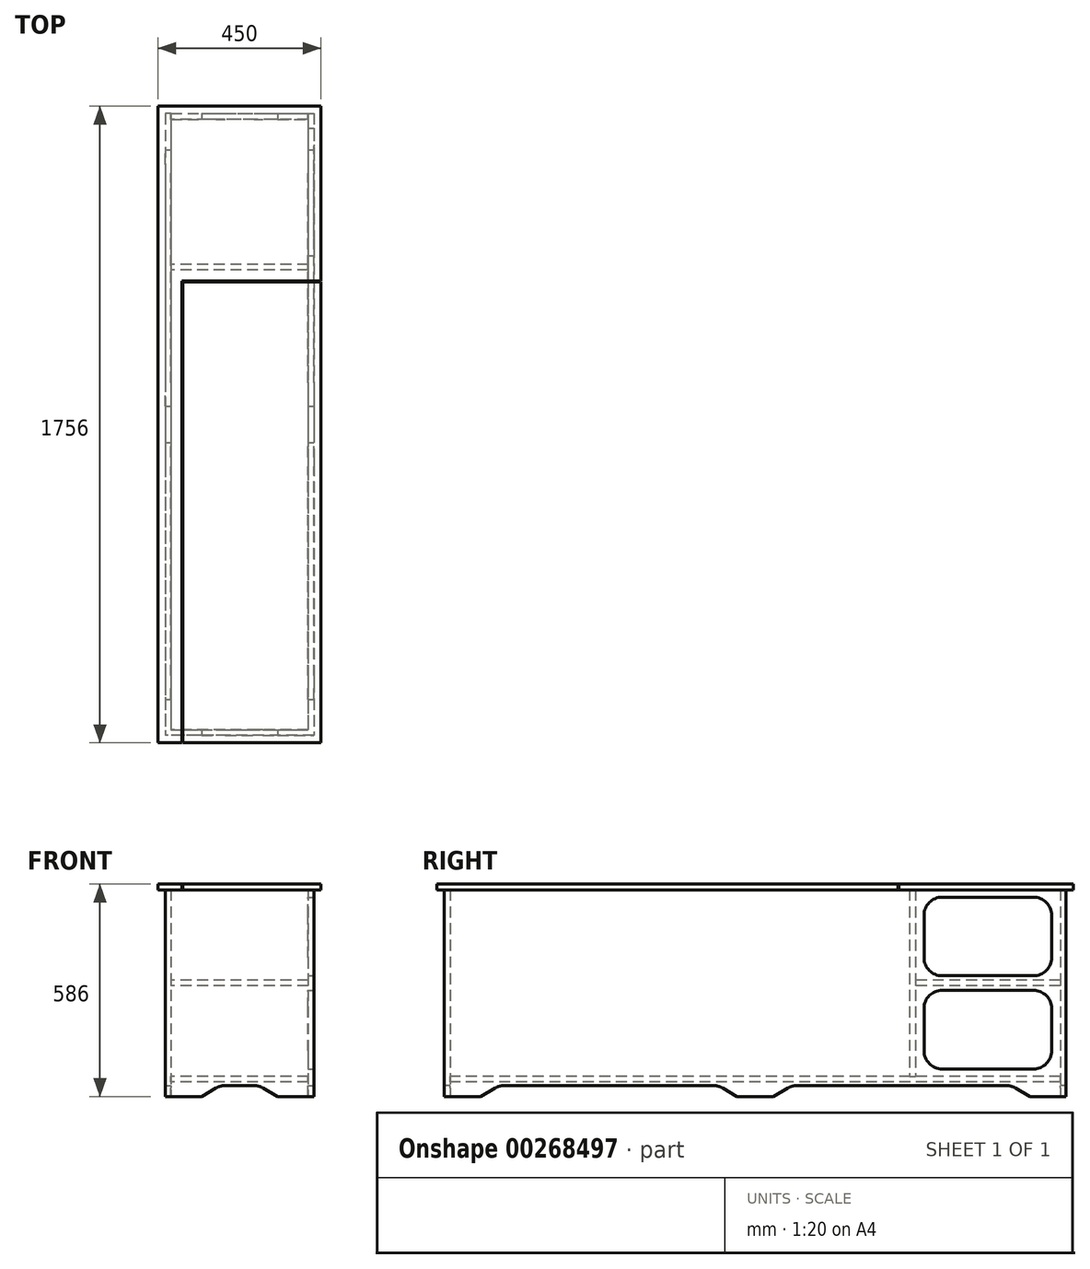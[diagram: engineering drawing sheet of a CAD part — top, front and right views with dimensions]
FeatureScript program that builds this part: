
annotation { "Feature Type Name" : "Feature", "Feature Type Description" : "" }
export const myFeature = defineFeature(function(context is Context, id is Id, definition is map)
    precondition{}
    {
        {
            var Q0;
            Q0=qCreatedBy(makeId("Right.planeOp"),FACE);
            var sketch = newSketch(context, id + "F0", { "sketchPlane" : qUnion([Q0])});
            skLineSegment(sketch, "E0.bottom", {"start": v(1716, 570) * mm, "end": v(0, 570) * mm});
            skLineSegment(sketch, "E0.top", {"start": v(1716, 0) * mm, "end": v(0, 0) * mm});
            skLineSegment(sketch, "E0.left", {"start": v(1716, 570) * mm, "end": v(1716, 0) * mm});
            skLineSegment(sketch, "E0.right", {"start": v(0, 570) * mm, "end": v(0, 0) * mm});
            skSolve(sketch);
        }
        {
            var Q0;
            Q0=makeQuery(id+"F0.imprint","IMPRINT",FACE,{"disambiguationData":[TD([[makeQuery(id+"F0.imprint","IMPRINT",EDGE,{"derivedFrom":sQuery(id+"F0.wireOp",EDGE,"E0.bottom")}),1.0]])]});
            extrude(context, id + "F1", {"entities" : qUnion([Q0]), "depth" : 16 * mm});
        }
        {
            var Q0;
            Q0=qCreatedBy(makeId("Right.planeOp"),FACE);
            cPlane(context, id + "F2", {"entities" : qUnion([Q0]), "cplaneType" : CPlaneType.OFFSET, "offset" : 410 * mm, "width" : 150 * mm, "height" : 150 * mm});
        }
        {
            var Q0;
            Q0=qCreatedBy(id+"F2.planeOp",FACE);
            var sketch = newSketch(context, id + "F3", { "sketchPlane" : qUnion([Q0])});
            skLineSegment(sketch, "E1.0", {"start": v(1716, 570) * mm, "end": v(0, 570) * mm});
            skLineSegment(sketch, "E2.0", {"start": v(0, 570) * mm, "end": v(0, 0) * mm});
            skLineSegment(sketch, "E3.0", {"start": v(1716, 0) * mm, "end": v(0, 0) * mm});
            skLineSegment(sketch, "E4.0", {"start": v(1716, 570) * mm, "end": v(1716, 0) * mm});
            skSolve(sketch);
        }
        {
            var Q0;
            Q0=makeQuery(id+"F3.imprint","IMPRINT",FACE,{"disambiguationData":[TD([[makeQuery(id+"F3.imprint","IMPRINT",EDGE,{"derivedFrom":sQuery(id+"F3.wireOp",EDGE,"E1.0")}),1.0]])]});
            extrude(context, id + "F4", {"entities" : qUnion([Q0]), "oppositeDirection" : true, "depth" : 16 * mm});
        }
        {
            var Q0;
            Q0=qCreatedBy(makeId("Front.planeOp"),FACE);
            var sketch = newSketch(context, id + "F5", { "sketchPlane" : qUnion([Q0])});
            skLineSegment(sketch, "E5.0", {"start": v(16, 570) * mm, "end": v(16, 0) * mm});
            skLineSegment(sketch, "E6.0", {"start": v(394, 570) * mm, "end": v(394, 0) * mm});
            skLineSegment(sketch, "E7", {"start": v(16, 570) * mm, "end": v(394, 570) * mm});
            skLineSegment(sketch, "E8", {"start": v(16, 0) * mm, "end": v(394, 0) * mm});
            skSolve(sketch);
        }
        {
            var Q0;
            Q0=makeQuery(id+"F5.imprint","IMPRINT",FACE,{"disambiguationData":[TD([[makeQuery(id+"F5.imprint","IMPRINT",EDGE,{"derivedFrom":sQuery(id+"F5.wireOp",EDGE,"E5.0")}),1.0]])]});
            extrude(context, id + "F6", {"entities" : qUnion([Q0]), "oppositeDirection" : true, "depth" : 16 * mm});
        }
        {
            var Q0;
            Q0=makeQuery(id+"F1.opExtrude","SWEPT_FACE",FACE,{"disambiguationData":[OSD([sQuery(id+"F0.wireOp",EDGE,"E0.left")])]});
            var sketch = newSketch(context, id + "F7", { "sketchPlane" : qUnion([Q0])});
            skLineSegment(sketch, "E9.0", {"start": v(-16, 570) * mm, "end": v(-394, 570) * mm});
            skLineSegment(sketch, "E10.0", {"start": v(-16, 0) * mm, "end": v(-394, 0) * mm});
            skLineSegment(sketch, "E11.0", {"start": v(-394, 570) * mm, "end": v(-394, 0) * mm});
            skLineSegment(sketch, "E12.0", {"start": v(-16, 570) * mm, "end": v(-16, 0) * mm});
            skSolve(sketch);
        }
        {
            var Q0;
            Q0=makeQuery(id+"F7.imprint","IMPRINT",FACE,{"disambiguationData":[TD([[makeQuery(id+"F7.imprint","IMPRINT",EDGE,{"derivedFrom":sQuery(id+"F7.wireOp",EDGE,"E9.0")}),1.0]])]});
            extrude(context, id + "F8", {"entities" : qUnion([Q0]), "oppositeDirection" : true, "depth" : 16 * mm});
        }
        {
            var Q0;
            Q0=makeQuery(id+"F1.opExtrude","SWEPT_FACE",FACE,{"disambiguationData":[OSD([sQuery(id+"F0.wireOp",EDGE,"E0.bottom")])]});
            var sketch = newSketch(context, id + "F9", { "sketchPlane" : qUnion([Q0])});
            skLineSegment(sketch, "E13.0", {"start": v(430, 1736) * mm, "end": v(430, -20) * mm});
            skLineSegment(sketch, "E14.0", {"start": v(-20, 1736) * mm, "end": v(-20, -20) * mm});
            skLineSegment(sketch, "E15.0", {"start": v(-20, -20) * mm, "end": v(430, -20) * mm});
            skLineSegment(sketch, "E16.0", {"start": v(-20, 1736) * mm, "end": v(430, 1736) * mm});
            skSolve(sketch);
        }
        {
            var Q0;
            Q0=makeQuery(id+"F9.imprint","IMPRINT",FACE,{"disambiguationData":[TD([[makeQuery(id+"F9.imprint","IMPRINT",EDGE,{"derivedFrom":sQuery(id+"F9.wireOp",EDGE,"E13.0")}),-1.0]])]});
            var Q1;
            {var subQ0=sQuery(id+"F0.wireOp",EDGE,"E0.bottom");Q1=makeQuery(id+"F9.imprint","IMPRINT",FACE,{"disambiguationData":[TD([[makeQuery(id+"F9.imprint","IMPRINT",EDGE,{"derivedFrom":makeQuery(id+"F1.opExtrude","CAP_EDGE",EDGE,{"disambiguationData":[OSD([subQ0])],"isStart":true})}),1.0]])]});}
            extrude(context, id + "F10", {"entities" : qUnion([Q0, Q1]), "depth" : 16 * mm});
        }
        {
            var Q0;
            Q0=makeQuery(id+"F1.opExtrude","CAP_FACE",FACE,{"disambiguationData":[OSD([sQuery(id+"F0.wireOp",EDGE,"E0.bottom"),sQuery(id+"F0.wireOp",EDGE,"E0.top"),sQuery(id+"F0.wireOp",EDGE,"E0.left"),sQuery(id+"F0.wireOp",EDGE,"E0.right")])],"isStart":false});
            var sketch = newSketch(context, id + "F11", { "sketchPlane" : qUnion([Q0])});
            skLineSegment(sketch, "E17.bottom", {"start": v(1700, 40) * mm, "end": v(16, 40) * mm});
            skLineSegment(sketch, "E17.top", {"start": v(1700, 56) * mm, "end": v(16, 56) * mm});
            skLineSegment(sketch, "E17.left", {"start": v(1700, 40) * mm, "end": v(1700, 56) * mm});
            skLineSegment(sketch, "E17.right", {"start": v(16, 40) * mm, "end": v(16, 56) * mm});
            skSolve(sketch);
        }
        {
            var Q0;
            Q0 = qSketchRegion(id + "F11", true);
            var Q1;
            Q1=makeQuery(id+"F4.opExtrude","CAP_FACE",FACE,{"disambiguationData":[OSD([sQuery(id+"F3.wireOp",EDGE,"E1.0"),sQuery(id+"F3.wireOp",EDGE,"E2.0"),sQuery(id+"F3.wireOp",EDGE,"E3.0"),sQuery(id+"F3.wireOp",EDGE,"E4.0")])],"isStart":false});
            extrude(context, id + "F12", {"entities" : qUnion([Q0]), "endBound" : BoundingType.UP_TO_SURFACE, "endBoundEntityFace" : qUnion([Q1]), "depth" : 25 * mm});
        }
        {
            var Q0;
            Q0=makeQuery(id+"F1.opExtrude","CAP_FACE",FACE,{"disambiguationData":[OSD([sQuery(id+"F0.wireOp",EDGE,"E0.bottom"),sQuery(id+"F0.wireOp",EDGE,"E0.top"),sQuery(id+"F0.wireOp",EDGE,"E0.left"),sQuery(id+"F0.wireOp",EDGE,"E0.right")])],"isStart":false});
            var sketch = newSketch(context, id + "F13", { "sketchPlane" : qUnion([Q0])});
            skLineSegment(sketch, "E18.bottom", {"start": v(1284, 570) * mm, "end": v(1300, 570) * mm});
            skLineSegment(sketch, "E18.left", {"start": v(1284, 570) * mm, "end": v(1284, 56) * mm});
            skLineSegment(sketch, "E18.right", {"start": v(1300, 570) * mm, "end": v(1300, 56) * mm});
            skLineSegment(sketch, "E19", {"start": v(1284, 56) * mm, "end": v(1300, 56) * mm});
            skSolve(sketch);
        }
        {
            var Q0;
            Q0 = qSketchRegion(id + "F13", true);
            var Q1;
            Q1=sQuery(id+"F13.wireOp",EDGE,"E18.right");
            var Q2;
            Q2=makeQuery(id+"F4.opExtrude","CAP_FACE",FACE,{"disambiguationData":[OSD([sQuery(id+"F3.wireOp",EDGE,"E1.0"),sQuery(id+"F3.wireOp",EDGE,"E2.0"),sQuery(id+"F3.wireOp",EDGE,"E3.0"),sQuery(id+"F3.wireOp",EDGE,"E4.0")])],"isStart":false});
            extrude(context, id + "F14", {"entities" : qUnion([Q0]), "surfaceEntities" : qUnion([Q1]), "endBound" : BoundingType.UP_TO_SURFACE, "endBoundEntityFace" : qUnion([Q2]), "depth" : 25 * mm});
        }
        {
            var Q0;
            Q0=makeQuery(id+"F1.opExtrude","CAP_FACE",FACE,{"disambiguationData":[OSD([sQuery(id+"F0.wireOp",EDGE,"E0.bottom"),sQuery(id+"F0.wireOp",EDGE,"E0.top"),sQuery(id+"F0.wireOp",EDGE,"E0.left"),sQuery(id+"F0.wireOp",EDGE,"E0.right")])],"isStart":false});
            var sketch = newSketch(context, id + "F15", { "sketchPlane" : qUnion([Q0])});
            skLineSegment(sketch, "E20.bottom", {"start": v(1700, 321) * mm, "end": v(1300, 321) * mm});
            skLineSegment(sketch, "E20.top", {"start": v(1700, 305) * mm, "end": v(1300, 305) * mm});
            skLineSegment(sketch, "E20.left", {"start": v(1700, 321) * mm, "end": v(1700, 305) * mm});
            skLineSegment(sketch, "E20.right", {"start": v(1300, 321) * mm, "end": v(1300, 305) * mm});
            skSolve(sketch);
        }
        {
            var Q0;
            Q0 = qSketchRegion(id + "F15", true);
            var Q1;
            Q1=makeQuery(id+"F4.opExtrude","CAP_FACE",FACE,{"disambiguationData":[OSD([sQuery(id+"F3.wireOp",EDGE,"E1.0"),sQuery(id+"F3.wireOp",EDGE,"E2.0"),sQuery(id+"F3.wireOp",EDGE,"E3.0"),sQuery(id+"F3.wireOp",EDGE,"E4.0")])],"isStart":false});
            extrude(context, id + "F16", {"entities" : qUnion([Q0]), "endBound" : BoundingType.UP_TO_SURFACE, "endBoundEntityFace" : qUnion([Q1]), "depth" : 25 * mm});
        }
        {
            var Q0;
            Q0=makeQuery(id+"F4.opExtrude","CAP_FACE",FACE,{"disambiguationData":[OSD([sQuery(id+"F3.wireOp",EDGE,"E1.0"),sQuery(id+"F3.wireOp",EDGE,"E2.0"),sQuery(id+"F3.wireOp",EDGE,"E3.0"),sQuery(id+"F3.wireOp",EDGE,"E4.0")])],"isStart":true});
            var sketch = newSketch(context, id + "F17", { "sketchPlane" : qUnion([Q0])});
            skLineSegment(sketch, "E21", {"start": v(858, 570) * mm, "end": v(858, 0) * mm, "construction": true});
            skLineSegment(sketch, "E22", {"start": v(100, 0) * mm, "end": v(151.96, 30) * mm});
            skLineSegment(sketch, "E23.MirrorCS", {"start": v(1616, 0) * mm, "end": v(1564.04, 30) * mm});
            skLineSegment(sketch, "E24", {"start": v(151.96, 30) * mm, "end": v(756.04, 30) * mm});
            skLineSegment(sketch, "E25", {"start": v(100, 0) * mm, "end": v(808, 0) * mm});
            skLineSegment(sketch, "E26", {"start": v(756.04, 30) * mm, "end": v(808, 0) * mm});
            skLineSegment(sketch, "E27.MirrorCS", {"start": v(959.96, 30) * mm, "end": v(908, 0) * mm});
            skLineSegment(sketch, "E28.trimOffspring", {"start": v(959.96, 30) * mm, "end": v(1564.04, 30) * mm});
            skLineSegment(sketch, "E29.trimOffspring", {"start": v(908, 0) * mm, "end": v(1616, 0) * mm});
            skSolve(sketch);
        }
        {
            var Q0;
            Q0 = qSketchRegion(id + "F17", true);
            var Q1;
            Q1=makeQuery(id+"F1.opExtrude","CAP_FACE",FACE,{"disambiguationData":[OSD([sQuery(id+"F0.wireOp",EDGE,"E0.bottom"),sQuery(id+"F0.wireOp",EDGE,"E0.top"),sQuery(id+"F0.wireOp",EDGE,"E0.left"),sQuery(id+"F0.wireOp",EDGE,"E0.right")])],"isStart":true});
            extrude(context, id + "F18", {"entities" : qUnion([Q0]), "operationType" : NewBodyOperationType.REMOVE, "endBound" : BoundingType.UP_TO_SURFACE, "oppositeDirection" : true, "endBoundEntityFace" : qUnion([Q1]), "depth" : 25 * mm});
        }
        {
            var Q0;
            Q0=makeQuery(id+"F6.opExtrude","CAP_FACE",FACE,{"disambiguationData":[OSD([sQuery(id+"F5.wireOp",EDGE,"E5.0"),sQuery(id+"F5.wireOp",EDGE,"E6.0"),sQuery(id+"F5.wireOp",EDGE,"E7"),sQuery(id+"F5.wireOp",EDGE,"E8")])],"isStart":true});
            var sketch = newSketch(context, id + "F19", { "sketchPlane" : qUnion([Q0])});
            skLineSegment(sketch, "E30", {"start": v(100, 0) * mm, "end": v(151.96, 30) * mm});
            skLineSegment(sketch, "E31", {"start": v(151.96, 30) * mm, "end": v(258.04, 30) * mm});
            skLineSegment(sketch, "E32", {"start": v(258.04, 30) * mm, "end": v(310, 0) * mm});
            skLineSegment(sketch, "E33", {"start": v(310, 0) * mm, "end": v(100, 0) * mm});
            skSolve(sketch);
        }
        {
            var Q0;
            Q0 = qSketchRegion(id + "F19", true);
            var Q1;
            Q1=makeQuery(id+"F8.opExtrude","CAP_FACE",FACE,{"disambiguationData":[OSD([sQuery(id+"F7.wireOp",EDGE,"E9.0"),sQuery(id+"F7.wireOp",EDGE,"E10.0"),sQuery(id+"F7.wireOp",EDGE,"E11.0"),sQuery(id+"F7.wireOp",EDGE,"E12.0")])],"isStart":true});
            extrude(context, id + "F20", {"entities" : qUnion([Q0]), "operationType" : NewBodyOperationType.REMOVE, "endBound" : BoundingType.UP_TO_SURFACE, "oppositeDirection" : true, "endBoundEntityFace" : qUnion([Q1]), "depth" : 25 * mm});
        }
        {
            var Q0;
            {var subQ0=sQuery(id+"F3.wireOp",EDGE,"E4.0");var subQ1=sQuery(id+"F3.wireOp",EDGE,"E3.0");var subQ2=sQuery(id+"F3.wireOp",EDGE,"E2.0");var subQ3=sQuery(id+"F3.wireOp",EDGE,"E1.0");var subQ4=sQuery(id+"F17.wireOp",EDGE,"E22");var subQ5=sQuery(id+"F17.wireOp",EDGE,"E24");Q0=makeQuery(id+"F18.boolean.opBoolean","COPY",EDGE,{"disambiguationData":[TD([makeQuery(id+"F4.opExtrude","CAP_FACE",FACE,{"disambiguationData":[OSD([subQ3,subQ2,subQ1,subQ0])],"isStart":true})])],"derivedFrom":makeQuery(id+"F18.opExtrude","SWEPT_EDGE",EDGE,{"disambiguationData":[OSD([subQ4,subQ5])]})});}
            var Q1;
            {var subQ0=sQuery(id+"F0.wireOp",EDGE,"E0.right");var subQ1=sQuery(id+"F0.wireOp",EDGE,"E0.left");var subQ2=sQuery(id+"F0.wireOp",EDGE,"E0.top");var subQ3=sQuery(id+"F0.wireOp",EDGE,"E0.bottom");var subQ4=sQuery(id+"F17.wireOp",EDGE,"E24");var subQ5=sQuery(id+"F17.wireOp",EDGE,"E22");Q1=makeQuery(id+"F18.boolean.opBoolean","COPY",EDGE,{"disambiguationData":[TD([makeQuery(id+"F1.opExtrude","CAP_FACE",FACE,{"disambiguationData":[OSD([subQ3,subQ2,subQ1,subQ0])],"isStart":true})])],"derivedFrom":makeQuery(id+"F18.opExtrude","SWEPT_EDGE",EDGE,{"disambiguationData":[OSD([subQ5,subQ4])]})});}
            var Q2;
            {var subQ0=sQuery(id+"F3.wireOp",EDGE,"E4.0");var subQ1=sQuery(id+"F3.wireOp",EDGE,"E3.0");var subQ2=sQuery(id+"F3.wireOp",EDGE,"E2.0");var subQ3=sQuery(id+"F3.wireOp",EDGE,"E1.0");var subQ4=makeQuery(id+"F4.opExtrude","CAP_FACE",FACE,{"disambiguationData":[OSD([subQ3,subQ2,subQ1,subQ0])],"isStart":true});var subQ6=sQuery(id+"F17.wireOp",EDGE,"E24");var subQ8=sQuery(id+"F17.wireOp",EDGE,"E26");var subQ9=sQuery(id+"F17.wireOp",EDGE,"E22");var subQ10=sQuery(id+"F17.wireOp",EDGE,"E28.trimOffspring");var subQ11=sQuery(id+"F17.wireOp",EDGE,"E23.MirrorCS");Q2=qUnion([makeQuery(id+"F18.boolean.opBoolean","COPY",EDGE,{"disambiguationData":[TD([subQ4])],"derivedFrom":makeQuery(id+"F18.opExtrude","SWEPT_EDGE",EDGE,{"disambiguationData":[OSD([subQ11,subQ10])]})}),makeQuery(id+"F18.boolean.opBoolean","COPY",EDGE,{"disambiguationData":[TD([subQ4])],"derivedFrom":makeQuery(id+"F18.opExtrude","SWEPT_EDGE",EDGE,{"disambiguationData":[OSD([subQ9,subQ6])]})}),makeQuery(id+"F18.boolean.opBoolean","COPY",EDGE,{"disambiguationData":[TD([subQ4])],"derivedFrom":makeQuery(id+"F18.opExtrude","SWEPT_EDGE",EDGE,{"disambiguationData":[OSD([subQ6,subQ8])]})})]);}
            var Q3;
            {var subQ0=sQuery(id+"F0.wireOp",EDGE,"E0.right");var subQ1=sQuery(id+"F0.wireOp",EDGE,"E0.left");var subQ2=sQuery(id+"F0.wireOp",EDGE,"E0.top");var subQ3=sQuery(id+"F0.wireOp",EDGE,"E0.bottom");var subQ4=makeQuery(id+"F1.opExtrude","CAP_FACE",FACE,{"disambiguationData":[OSD([subQ3,subQ2,subQ1,subQ0])],"isStart":true});var subQ5=sQuery(id+"F17.wireOp",EDGE,"E24");var subQ8=sQuery(id+"F17.wireOp",EDGE,"E26");var subQ9=sQuery(id+"F17.wireOp",EDGE,"E22");var subQ10=sQuery(id+"F17.wireOp",EDGE,"E23.MirrorCS");var subQ11=sQuery(id+"F17.wireOp",EDGE,"E28.trimOffspring");Q3=qUnion([makeQuery(id+"F18.boolean.opBoolean","COPY",EDGE,{"disambiguationData":[TD([subQ4])],"derivedFrom":makeQuery(id+"F18.opExtrude","SWEPT_EDGE",EDGE,{"disambiguationData":[OSD([subQ10,subQ11])]})}),makeQuery(id+"F18.boolean.opBoolean","COPY",EDGE,{"disambiguationData":[TD([subQ4])],"derivedFrom":makeQuery(id+"F18.opExtrude","SWEPT_EDGE",EDGE,{"disambiguationData":[OSD([subQ9,subQ5])]})}),makeQuery(id+"F18.boolean.opBoolean","COPY",EDGE,{"disambiguationData":[TD([subQ4])],"derivedFrom":makeQuery(id+"F18.opExtrude","SWEPT_EDGE",EDGE,{"disambiguationData":[OSD([subQ5,subQ8])]})})]);}
            var Q4;
            {var subQ0=sQuery(id+"F3.wireOp",EDGE,"E4.0");var subQ1=sQuery(id+"F3.wireOp",EDGE,"E3.0");var subQ2=sQuery(id+"F3.wireOp",EDGE,"E2.0");var subQ3=sQuery(id+"F3.wireOp",EDGE,"E1.0");var subQ4=sQuery(id+"F17.wireOp",EDGE,"E28.trimOffspring");var subQ5=sQuery(id+"F17.wireOp",EDGE,"E27.MirrorCS");Q4=makeQuery(id+"F18.boolean.opBoolean","COPY",EDGE,{"disambiguationData":[TD([makeQuery(id+"F4.opExtrude","CAP_FACE",FACE,{"disambiguationData":[OSD([subQ3,subQ2,subQ1,subQ0])],"isStart":true})])],"derivedFrom":makeQuery(id+"F18.opExtrude","SWEPT_EDGE",EDGE,{"disambiguationData":[OSD([subQ5,subQ4])]})});}
            var Q5;
            {var subQ0=sQuery(id+"F0.wireOp",EDGE,"E0.right");var subQ1=sQuery(id+"F0.wireOp",EDGE,"E0.left");var subQ2=sQuery(id+"F0.wireOp",EDGE,"E0.top");var subQ3=sQuery(id+"F0.wireOp",EDGE,"E0.bottom");var subQ4=sQuery(id+"F17.wireOp",EDGE,"E27.MirrorCS");var subQ5=sQuery(id+"F17.wireOp",EDGE,"E28.trimOffspring");Q5=makeQuery(id+"F18.boolean.opBoolean","COPY",EDGE,{"disambiguationData":[TD([makeQuery(id+"F1.opExtrude","CAP_FACE",FACE,{"disambiguationData":[OSD([subQ3,subQ2,subQ1,subQ0])],"isStart":true})])],"derivedFrom":makeQuery(id+"F18.opExtrude","SWEPT_EDGE",EDGE,{"disambiguationData":[OSD([subQ4,subQ5])]})});}
            var Q6;
            {var subQ0=sQuery(id+"F7.wireOp",EDGE,"E12.0");var subQ1=sQuery(id+"F7.wireOp",EDGE,"E11.0");var subQ2=sQuery(id+"F7.wireOp",EDGE,"E10.0");var subQ3=sQuery(id+"F7.wireOp",EDGE,"E9.0");var subQ4=sQuery(id+"F19.wireOp",EDGE,"E31");var subQ5=sQuery(id+"F19.wireOp",EDGE,"E30");Q6=makeQuery(id+"F20.boolean.opBoolean","COPY",EDGE,{"disambiguationData":[TD([makeQuery(id+"F8.opExtrude","CAP_FACE",FACE,{"disambiguationData":[OSD([subQ3,subQ2,subQ1,subQ0])],"isStart":true})])],"derivedFrom":makeQuery(id+"F20.opExtrude","SWEPT_EDGE",EDGE,{"disambiguationData":[OSD([subQ5,subQ4])]})});}
            var Q7;
            {var subQ0=sQuery(id+"F7.wireOp",EDGE,"E12.0");var subQ1=sQuery(id+"F7.wireOp",EDGE,"E11.0");var subQ2=sQuery(id+"F7.wireOp",EDGE,"E10.0");var subQ3=sQuery(id+"F7.wireOp",EDGE,"E9.0");var subQ4=sQuery(id+"F19.wireOp",EDGE,"E31");var subQ5=sQuery(id+"F19.wireOp",EDGE,"E32");Q7=makeQuery(id+"F20.boolean.opBoolean","COPY",EDGE,{"disambiguationData":[TD([makeQuery(id+"F8.opExtrude","CAP_FACE",FACE,{"disambiguationData":[OSD([subQ3,subQ2,subQ1,subQ0])],"isStart":true})])],"derivedFrom":makeQuery(id+"F20.opExtrude","SWEPT_EDGE",EDGE,{"disambiguationData":[OSD([subQ4,subQ5])]})});}
            var Q8;
            {var subQ0=sQuery(id+"F5.wireOp",EDGE,"E8");var subQ1=sQuery(id+"F5.wireOp",EDGE,"E7");var subQ2=sQuery(id+"F5.wireOp",EDGE,"E6.0");var subQ3=sQuery(id+"F5.wireOp",EDGE,"E5.0");var subQ4=sQuery(id+"F19.wireOp",EDGE,"E32");var subQ5=sQuery(id+"F19.wireOp",EDGE,"E31");Q8=makeQuery(id+"F20.boolean.opBoolean","COPY",EDGE,{"disambiguationData":[TD([makeQuery(id+"F6.opExtrude","CAP_FACE",FACE,{"disambiguationData":[OSD([subQ3,subQ2,subQ1,subQ0])],"isStart":true})])],"derivedFrom":makeQuery(id+"F20.opExtrude","SWEPT_EDGE",EDGE,{"disambiguationData":[OSD([subQ5,subQ4])]})});}
            var Q9;
            {var subQ0=sQuery(id+"F5.wireOp",EDGE,"E8");var subQ1=sQuery(id+"F5.wireOp",EDGE,"E7");var subQ2=sQuery(id+"F5.wireOp",EDGE,"E6.0");var subQ3=sQuery(id+"F5.wireOp",EDGE,"E5.0");var subQ4=sQuery(id+"F19.wireOp",EDGE,"E30");var subQ5=sQuery(id+"F19.wireOp",EDGE,"E31");Q9=makeQuery(id+"F20.boolean.opBoolean","COPY",EDGE,{"disambiguationData":[TD([makeQuery(id+"F6.opExtrude","CAP_FACE",FACE,{"disambiguationData":[OSD([subQ3,subQ2,subQ1,subQ0])],"isStart":true})])],"derivedFrom":makeQuery(id+"F20.opExtrude","SWEPT_EDGE",EDGE,{"disambiguationData":[OSD([subQ4,subQ5])]})});}
            fillet(context, id + "F21", {"entities" : qUnion([Q0, Q1, Q2, Q3, Q4, Q5, Q6, Q7, Q8, Q9]), "radius" : 50 * mm, "tangentPropagation" : true, "allowEdgeOverflow" : false});
        }
        {
            var Q0;
            Q0=makeQuery(id+"F4.opExtrude","CAP_FACE",FACE,{"disambiguationData":[OSD([sQuery(id+"F3.wireOp",EDGE,"E1.0"),sQuery(id+"F3.wireOp",EDGE,"E2.0"),sQuery(id+"F3.wireOp",EDGE,"E3.0"),sQuery(id+"F3.wireOp",EDGE,"E4.0")])],"isStart":true});
            var sketch = newSketch(context, id + "F22", { "sketchPlane" : qUnion([Q0])});
            skLineSegment(sketch, "E34.bottom", {"start": v(1324, 550) * mm, "end": v(1676, 550) * mm});
            skLineSegment(sketch, "E34.top", {"start": v(1324, 333) * mm, "end": v(1676, 333) * mm});
            skLineSegment(sketch, "E34.left", {"start": v(1324, 550) * mm, "end": v(1324, 333) * mm});
            skLineSegment(sketch, "E34.right", {"start": v(1676, 550) * mm, "end": v(1676, 333) * mm});
            skLineSegment(sketch, "E35.bottom", {"start": v(1324, 293) * mm, "end": v(1676, 293) * mm});
            skLineSegment(sketch, "E35.top", {"start": v(1324, 76) * mm, "end": v(1676, 76) * mm});
            skLineSegment(sketch, "E35.left", {"start": v(1324, 293) * mm, "end": v(1324, 76) * mm});
            skLineSegment(sketch, "E35.right", {"start": v(1676, 293) * mm, "end": v(1676, 76) * mm});
            skLineSegment(sketch, "E36", {"start": v(1500, 570) * mm, "end": v(1500, 321) * mm, "construction": true});
            skLineSegment(sketch, "E37", {"start": v(1300, 313) * mm, "end": v(1700, 313) * mm, "construction": true});
            skSolve(sketch);
        }
        {
            var Q0;
            Q0 = qSketchRegion(id + "F22", true);
            var Q1;
            Q1=makeQuery(id+"F4.opExtrude","CAP_FACE",FACE,{"disambiguationData":[OSD([sQuery(id+"F3.wireOp",EDGE,"E1.0"),sQuery(id+"F3.wireOp",EDGE,"E2.0"),sQuery(id+"F3.wireOp",EDGE,"E3.0"),sQuery(id+"F3.wireOp",EDGE,"E4.0")])],"isStart":false});
            extrude(context, id + "F23", {"entities" : qUnion([Q0]), "operationType" : NewBodyOperationType.REMOVE, "endBound" : BoundingType.UP_TO_SURFACE, "oppositeDirection" : true, "endBoundEntityFace" : qUnion([Q1]), "depth" : 25 * mm});
        }
        {
            var Q0;
            Q0=makeQuery(id+"F23.boolean.opBoolean","COPY",EDGE,{"derivedFrom":makeQuery(id+"F23.opExtrude","SWEPT_EDGE",EDGE,{"disambiguationData":[OSD([sQuery(id+"F22.wireOp",EDGE,"E34.top"),sQuery(id+"F22.wireOp",EDGE,"E34.right")])]})});
            var Q1;
            Q1=makeQuery(id+"F23.boolean.opBoolean","COPY",EDGE,{"derivedFrom":makeQuery(id+"F23.opExtrude","SWEPT_EDGE",EDGE,{"disambiguationData":[OSD([sQuery(id+"F22.wireOp",EDGE,"E35.top"),sQuery(id+"F22.wireOp",EDGE,"E35.right")])]})});
            var Q2;
            Q2=makeQuery(id+"F23.boolean.opBoolean","COPY",EDGE,{"derivedFrom":makeQuery(id+"F23.opExtrude","SWEPT_EDGE",EDGE,{"disambiguationData":[OSD([sQuery(id+"F22.wireOp",EDGE,"E35.bottom"),sQuery(id+"F22.wireOp",EDGE,"E35.right")])]})});
            var Q3;
            Q3=makeQuery(id+"F23.boolean.opBoolean","COPY",EDGE,{"derivedFrom":makeQuery(id+"F23.opExtrude","SWEPT_EDGE",EDGE,{"disambiguationData":[OSD([sQuery(id+"F22.wireOp",EDGE,"E34.bottom"),sQuery(id+"F22.wireOp",EDGE,"E34.right")])]})});
            var Q4;
            Q4=makeQuery(id+"F23.boolean.opBoolean","COPY",EDGE,{"derivedFrom":makeQuery(id+"F23.opExtrude","SWEPT_EDGE",EDGE,{"disambiguationData":[OSD([sQuery(id+"F22.wireOp",EDGE,"E34.bottom"),sQuery(id+"F22.wireOp",EDGE,"E34.left")])]})});
            var Q5;
            Q5=makeQuery(id+"F23.boolean.opBoolean","COPY",EDGE,{"derivedFrom":makeQuery(id+"F23.opExtrude","SWEPT_EDGE",EDGE,{"disambiguationData":[OSD([sQuery(id+"F22.wireOp",EDGE,"E35.bottom"),sQuery(id+"F22.wireOp",EDGE,"E35.left")])]})});
            var Q6;
            Q6=makeQuery(id+"F23.boolean.opBoolean","COPY",EDGE,{"derivedFrom":makeQuery(id+"F23.opExtrude","SWEPT_EDGE",EDGE,{"disambiguationData":[OSD([sQuery(id+"F22.wireOp",EDGE,"E34.top"),sQuery(id+"F22.wireOp",EDGE,"E34.left")])]})});
            var Q7;
            Q7=makeQuery(id+"F23.boolean.opBoolean","COPY",EDGE,{"derivedFrom":makeQuery(id+"F23.opExtrude","SWEPT_EDGE",EDGE,{"disambiguationData":[OSD([sQuery(id+"F22.wireOp",EDGE,"E35.top"),sQuery(id+"F22.wireOp",EDGE,"E35.left")])]})});
            fillet(context, id + "F24", {"entities" : qUnion([Q0, Q1, Q2, Q3, Q4, Q5, Q6, Q7]), "radius" : 50 * mm, "tangentPropagation" : true, "allowEdgeOverflow" : false});
        }
        {
            var Q0;
            Q0=makeQuery(id+"F10.opExtrude","CAP_FACE",FACE,{"disambiguationData":[OSD([sQuery(id+"F9.wireOp",EDGE,"E13.0"),sQuery(id+"F9.wireOp",EDGE,"E14.0"),sQuery(id+"F9.wireOp",EDGE,"E15.0"),sQuery(id+"F9.wireOp",EDGE,"E16.0")])],"isStart":false});
            var sketch = newSketch(context, id + "F25", { "sketchPlane" : qUnion([Q0])});
            skLineSegment(sketch, "E38", {"start": v(430, 1254) * mm, "end": v(46, 1254) * mm});
            skLineSegment(sketch, "E39", {"start": v(46, 1254) * mm, "end": v(46, -20) * mm});
            skLineSegment(sketch, "E40", {"start": v(46, -20) * mm, "end": v(48, -20) * mm});
            skLineSegment(sketch, "E41", {"start": v(48, -20) * mm, "end": v(48, 1252) * mm});
            skLineSegment(sketch, "E42", {"start": v(48, 1252) * mm, "end": v(430, 1252) * mm});
            skLineSegment(sketch, "E43", {"start": v(430, 1252) * mm, "end": v(430, 1254) * mm});
            skSolve(sketch);
        }
        {
            var Q0;
            Q0 = qSketchRegion(id + "F25", true);
            var Q1;
            Q1=makeQuery(id+"F10.opExtrude","CAP_FACE",FACE,{"disambiguationData":[OSD([sQuery(id+"F9.wireOp",EDGE,"E13.0"),sQuery(id+"F9.wireOp",EDGE,"E14.0"),sQuery(id+"F9.wireOp",EDGE,"E15.0"),sQuery(id+"F9.wireOp",EDGE,"E16.0")])],"isStart":true});
            extrude(context, id + "F26", {"entities" : qUnion([Q0]), "operationType" : NewBodyOperationType.REMOVE, "endBound" : BoundingType.UP_TO_SURFACE, "oppositeDirection" : true, "endBoundEntityFace" : qUnion([Q1]), "depth" : 25 * mm});
        }
        {
            var Q0;
            Q0=makeQuery(id+"F6.opExtrude","CAP_FACE",FACE,{"disambiguationData":[OSD([sQuery(id+"F5.wireOp",EDGE,"E5.0"),sQuery(id+"F5.wireOp",EDGE,"E6.0"),sQuery(id+"F5.wireOp",EDGE,"E7"),sQuery(id+"F5.wireOp",EDGE,"E8")])],"isStart":true});
            var sketch = newSketch(context, id + "F27", { "sketchPlane" : qUnion([Q0])});
            skLineSegment(sketch, "E44.bottom", {"start": v(394, 504) * mm, "end": v(410, 504) * mm});
            skLineSegment(sketch, "E44.top", {"start": v(394, 444) * mm, "end": v(410, 444) * mm});
            skLineSegment(sketch, "E44.left", {"start": v(394, 504) * mm, "end": v(394, 444) * mm});
            skLineSegment(sketch, "E44.right", {"start": v(410, 504) * mm, "end": v(410, 444) * mm});
            skLineSegment(sketch, "E45.bottom", {"start": v(394, 378) * mm, "end": v(410, 378) * mm});
            skLineSegment(sketch, "E45.top", {"start": v(394, 318) * mm, "end": v(410, 318) * mm});
            skLineSegment(sketch, "E45.left", {"start": v(394, 378) * mm, "end": v(394, 318) * mm});
            skLineSegment(sketch, "E45.right", {"start": v(410, 378) * mm, "end": v(410, 318) * mm});
            skLineSegment(sketch, "E46.bottom", {"start": v(394, 252) * mm, "end": v(410, 252) * mm});
            skLineSegment(sketch, "E46.top", {"start": v(394, 192) * mm, "end": v(410, 192) * mm});
            skLineSegment(sketch, "E46.left", {"start": v(394, 252) * mm, "end": v(394, 192) * mm});
            skLineSegment(sketch, "E46.right", {"start": v(410, 252) * mm, "end": v(410, 192) * mm});
            skLineSegment(sketch, "E47.bottom", {"start": v(394, 126) * mm, "end": v(410, 126) * mm});
            skLineSegment(sketch, "E47.top", {"start": v(394, 66) * mm, "end": v(410, 66) * mm});
            skLineSegment(sketch, "E47.left", {"start": v(394, 126) * mm, "end": v(394, 66) * mm});
            skLineSegment(sketch, "E47.right", {"start": v(410, 126) * mm, "end": v(410, 66) * mm});
            skLineSegment(sketch, "E48", {"start": v(205, 30) * mm, "end": v(205, 570) * mm, "construction": true});
            skLineSegment(sketch, "E49.MirrorCS", {"start": v(0, 126) * mm, "end": v(0, 66) * mm});
            skLineSegment(sketch, "E50.MirrorCS", {"start": v(16, 444) * mm, "end": v(0, 444) * mm});
            skLineSegment(sketch, "E51.MirrorCS", {"start": v(0, 252) * mm, "end": v(0, 192) * mm});
            skLineSegment(sketch, "E52.MirrorCS", {"start": v(0, 504) * mm, "end": v(0, 444) * mm});
            skLineSegment(sketch, "E53.MirrorCS", {"start": v(16, 318) * mm, "end": v(0, 318) * mm});
            skLineSegment(sketch, "E54.MirrorCS", {"start": v(16, 252) * mm, "end": v(0, 252) * mm});
            skLineSegment(sketch, "E55.MirrorCS", {"start": v(16, 126) * mm, "end": v(16, 66) * mm});
            skLineSegment(sketch, "E56.MirrorCS", {"start": v(16, 504) * mm, "end": v(0, 504) * mm});
            skLineSegment(sketch, "E57.MirrorCS", {"start": v(16, 252) * mm, "end": v(16, 192) * mm});
            skLineSegment(sketch, "E58.MirrorCS", {"start": v(16, 504) * mm, "end": v(16, 444) * mm});
            skLineSegment(sketch, "E59.MirrorCS", {"start": v(16, 126) * mm, "end": v(0, 126) * mm});
            skLineSegment(sketch, "E60.MirrorCS", {"start": v(16, 378) * mm, "end": v(0, 378) * mm});
            skLineSegment(sketch, "E61.MirrorCS", {"start": v(0, 378) * mm, "end": v(0, 318) * mm});
            skLineSegment(sketch, "E62.MirrorCS", {"start": v(16, 66) * mm, "end": v(0, 66) * mm});
            skLineSegment(sketch, "E63.MirrorCS", {"start": v(16, 378) * mm, "end": v(16, 318) * mm});
            skLineSegment(sketch, "E64.MirrorCS", {"start": v(16, 192) * mm, "end": v(0, 192) * mm});
            skSolve(sketch);
        }
        {
            var Q0;
            Q0 = qSketchRegion(id + "F27", true);
            var Q1;
            Q1=makeQuery(id+"F6.opExtrude","CAP_FACE",FACE,{"disambiguationData":[OSD([sQuery(id+"F5.wireOp",EDGE,"E5.0"),sQuery(id+"F5.wireOp",EDGE,"E6.0"),sQuery(id+"F5.wireOp",EDGE,"E7"),sQuery(id+"F5.wireOp",EDGE,"E8")])],"isStart":false});
            extrude(context, id + "F28", {"entities" : qUnion([Q0]), "operationType" : NewBodyOperationType.ADD, "endBound" : BoundingType.UP_TO_SURFACE, "oppositeDirection" : true, "endBoundEntityFace" : qUnion([Q1]), "depth" : 25 * mm});
        }
    });
